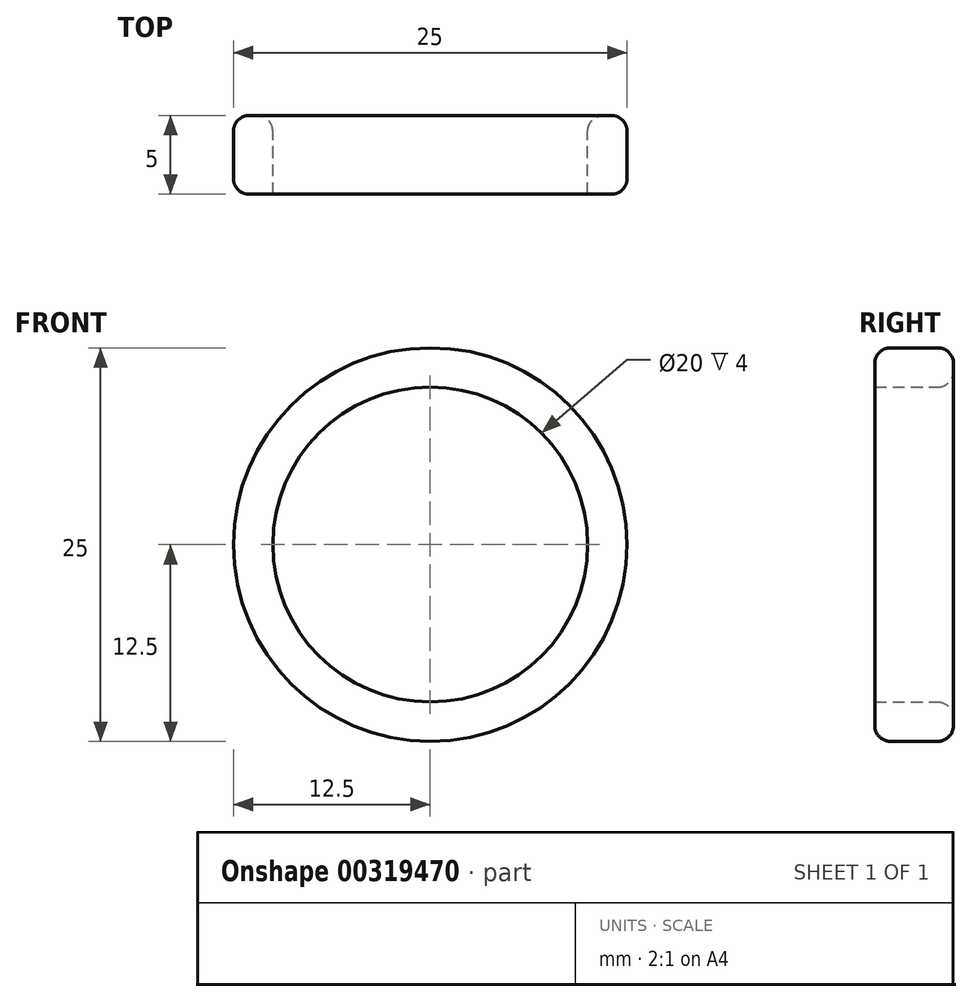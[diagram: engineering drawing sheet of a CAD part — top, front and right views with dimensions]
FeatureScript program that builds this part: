
annotation { "Feature Type Name" : "Feature", "Feature Type Description" : "" }
export const myFeature = defineFeature(function(context is Context, id is Id, definition is map)
    precondition{}
    {
        {
            var Q0;
            Q0=qCreatedBy(makeId("Front.planeOp"),FACE);
            var sketch = newSketch(context, id + "F0", { "sketchPlane" : qUnion([Q0])});
            skCircle(sketch, "E0", {"center": v(0, 0) * mm, "radius": 10 * mm});
            skCircle(sketch, "E1", {"center": v(0, 0) * mm, "radius": 12.5 * mm});
            skSolve(sketch);
        }
        {
            var Q0;
            Q0 = qSketchRegion(id + "F0", true);
            extrude(context, id + "F1", {"entities" : qUnion([Q0]), "depth" : 5 * mm});
        }
        {
            var Q0;
            Q0=makeQuery(id+"F1.opExtrude","CAP_EDGE",EDGE,{"disambiguationData":[OSD([sQuery(id+"F0.wireOp",EDGE,"E1")])],"isStart":false});
            var Q1;
            Q1=makeQuery(id+"F1.opExtrude","CAP_EDGE",EDGE,{"disambiguationData":[OSD([sQuery(id+"F0.wireOp",EDGE,"E1")])],"isStart":true});
            var Q2;
            Q2=makeQuery(id+"F1.opExtrude","CAP_EDGE",EDGE,{"disambiguationData":[OSD([sQuery(id+"F0.wireOp",EDGE,"E0")])],"isStart":true});
            fillet(context, id + "F2", {"entities" : qUnion([Q0, Q1, Q2]), "radius" : 1 * mm, "tangentPropagation" : true, "allowEdgeOverflow" : false});
        }
    });
